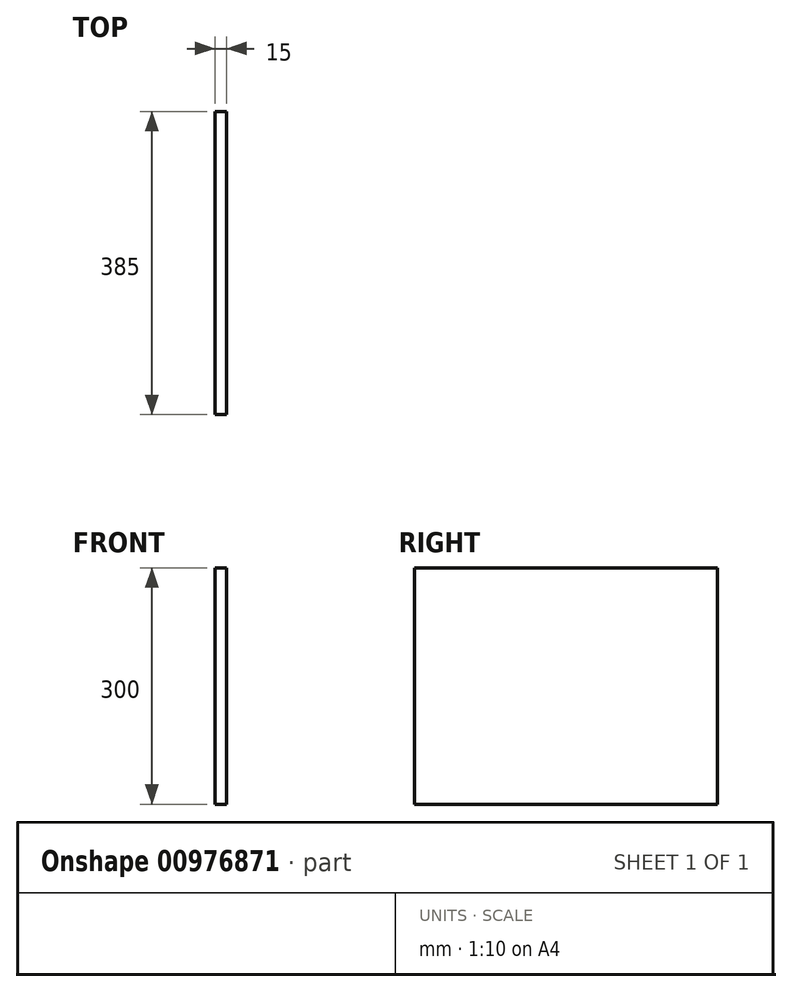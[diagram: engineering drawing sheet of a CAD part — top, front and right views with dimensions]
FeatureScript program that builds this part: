
annotation { "Feature Type Name" : "Feature", "Feature Type Description" : "" }
export const myFeature = defineFeature(function(context is Context, id is Id, definition is map)
    precondition{}
    {
        {
            var Q0;
            Q0=qCreatedBy(makeId("Right.planeOp"),FACE);
            var sketch = newSketch(context, id + "F0", { "sketchPlane" : qUnion([Q0])});
            skLineSegment(sketch, "E0.bottom", {"start": v(-192.5, 150) * mm, "end": v(192.5, 150) * mm});
            skLineSegment(sketch, "E0.top", {"start": v(-192.5, -150) * mm, "end": v(192.5, -150) * mm});
            skLineSegment(sketch, "E0.left", {"start": v(-192.5, 150) * mm, "end": v(-192.5, -150) * mm});
            skLineSegment(sketch, "E0.right", {"start": v(192.5, 150) * mm, "end": v(192.5, -150) * mm});
            skPoint(sketch, "E0.middle", {"position": v(0, 0) * mm});
            skSolve(sketch);
        }
        {
            var Q0;
            Q0 = qSketchRegion(id + "F0", true);
            extrude(context, id + "F1", {"entities" : qUnion([Q0]), "depth" : 15 * mm, "offsetDistance" : 25 * mm});
        }
    });
